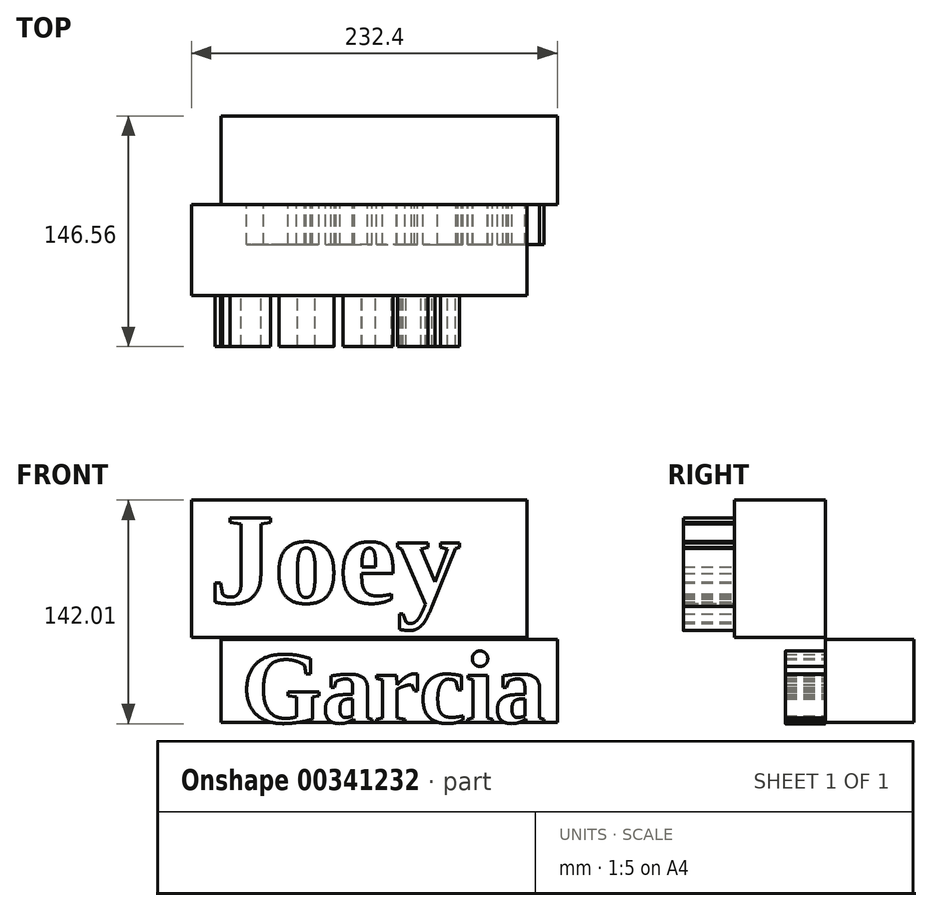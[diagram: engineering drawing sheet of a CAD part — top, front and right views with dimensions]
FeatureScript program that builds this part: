
annotation { "Feature Type Name" : "Feature", "Feature Type Description" : "" }
export const myFeature = defineFeature(function(context is Context, id is Id, definition is map)
    precondition{}
    {
        {
            var Q0;
            Q0=qCreatedBy(makeId("Front.planeOp"),FACE);
            var sketch = newSketch(context, id + "F0", { "sketchPlane" : qUnion([Q0])});
            skLineSegment(sketch, "E0.bottom", {"start": v(-34.18, -23.42) * mm, "end": v(179.49, -23.42) * mm});
            skLineSegment(sketch, "E0.top", {"start": v(-34.18, -76.24) * mm, "end": v(179.49, -76.24) * mm});
            skLineSegment(sketch, "E0.left", {"start": v(-34.18, -23.42) * mm, "end": v(-34.18, -76.24) * mm});
            skLineSegment(sketch, "E0.right", {"start": v(179.49, -23.42) * mm, "end": v(179.49, -76.24) * mm});
            skSolve(sketch);
        }
        {
            var Q0;
            Q0 = qSketchRegion(id + "F0", true);
            extrude(context, id + "F1", {"entities" : qUnion([Q0]), "oppositeDirection" : true, "depth" : 56.4 * mm});
        }
        {
            var Q0;
            Q0=makeQuery(id+"F1.opExtrude","CAP_FACE",FACE,{"disambiguationData":[OSD([sQuery(id+"F0.wireOp",EDGE,"E0.bottom"),sQuery(id+"F0.wireOp",EDGE,"E0.top"),sQuery(id+"F0.wireOp",EDGE,"E0.left"),sQuery(id+"F0.wireOp",EDGE,"E0.right")])],"isStart":true});
            var sketch = newSketch(context, id + "F2", { "sketchPlane" : qUnion([Q0])});
            skText(sketch, "E1", { "text": "Garcia", "fontName": "Tinos-Bold.ttf"});
            const initialGuessF2  = {"E1": [-0.021, -0.07624, 1, 0, 0.04724]};
            skSetInitialGuess(sketch, initialGuessF2);
            skSolve(sketch);
        }
        {
            var Q0;
            Q0 = qSketchRegion(id + "F2", true);
            extrude(context, id + "F3", {"entities" : qUnion([Q0]), "operationType" : NewBodyOperationType.ADD, "depth" : 25.4 * mm});
        }
        {
            var Q0;
            Q0=qCreatedBy(makeId("Front.planeOp"),FACE);
            var sketch = newSketch(context, id + "F4", { "sketchPlane" : qUnion([Q0])});
            skLineSegment(sketch, "E2.bottom", {"start": v(-52.9, 0) * mm, "end": v(160.23, 0) * mm});
            skLineSegment(sketch, "E2.top", {"start": v(-52.9, 65.12) * mm, "end": v(160.23, 65.12) * mm});
            skLineSegment(sketch, "E2.left", {"start": v(-52.9, 0) * mm, "end": v(-52.9, 65.12) * mm});
            skLineSegment(sketch, "E2.right", {"start": v(160.23, 0) * mm, "end": v(160.23, 65.12) * mm});
            skSolve(sketch);
        }
        {
            var Q0;
            Q0 = qSketchRegion(id + "F4", true);
            extrude(context, id + "F5", {"entities" : qUnion([Q0]), "depth" : 57.66 * mm});
        }
        {
            var Q0;
            Q0=makeQuery(id+"F5.opExtrude","CAP_FACE",FACE,{"disambiguationData":[OSD([sQuery(id+"F4.wireOp",EDGE,"E2.bottom"),sQuery(id+"F4.wireOp",EDGE,"E2.top"),sQuery(id+"F4.wireOp",EDGE,"E2.left"),sQuery(id+"F4.wireOp",EDGE,"E2.right")])],"isStart":false});
            var sketch = newSketch(context, id + "F6", { "sketchPlane" : qUnion([Q0])});
            skText(sketch, "E3", { "text": "Joey", "fontName": "Tinos-Bold.ttf"});
            const initialGuessF6  = {"E3": [-0.0416, 0, 1, 0, 0.05923]};
            skSetInitialGuess(sketch, initialGuessF6);
            skSolve(sketch);
        }
        {
            var Q0;
            Q0 = qSketchRegion(id + "F6", true);
            extrude(context, id + "F7", {"entities" : qUnion([Q0]), "operationType" : NewBodyOperationType.ADD, "depth" : 32.5 * mm});
        }
        {
            var Q0;
            Q0=makeQuery(id+"F5.opExtrude","SWEPT_FACE",FACE,{"disambiguationData":[OSD([sQuery(id+"F4.wireOp",EDGE,"E2.bottom")])]});
            extrude(context, id + "F8", {"entities" : qUnion([Q0]), "operationType" : NewBodyOperationType.ADD, "depth" : 13.72 * mm});
        }
        {
            var Q0;
            Q0=makeQuery(id+"F8.opExtrude","CAP_FACE",FACE,{"disambiguationData":[OSD([sQuery(id+"F4.wireOp",EDGE,"E2.bottom")])],"isStart":false});
            extrude(context, id + "F9", {"entities" : qUnion([Q0]), "operationType" : NewBodyOperationType.ADD, "depth" : 8.38 * mm});
        }
    });
